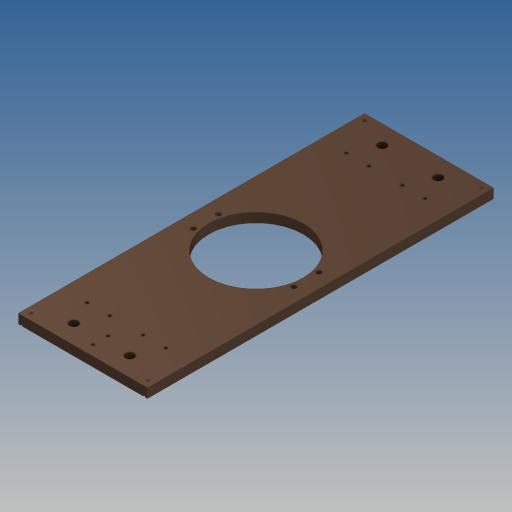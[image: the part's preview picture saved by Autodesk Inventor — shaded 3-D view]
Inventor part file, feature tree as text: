
AUTODESK INVENTOR PART (.ipt)
format: ipt  version: 2023.3 (Build 273359000, 359)  size: 237,056 bytes
history: native  units: mm
features: sketch x8, hole x6, extrude x2
ambient origin geometry x8: Origin, YZ Plane, XZ Plane, XY Plane, X Axis, Y Axis, Z Axis, Center Point
bodies: Body1 (feature_tree)
feature tree (16):
  extrude  "Extrusion1"  Depth=205.0mm
  hole  "Bohrung1"  [1 undecoded]
  extrude  "Extrusion2"  Depth=530.0mm
  hole  "Bohrung6"  [1 undecoded]
  hole  "Bohrung7"  [1 undecoded]
  hole  "Bohrung8"  [1 undecoded]
  hole  "Bohrung9"  [1 undecoded]
  hole  "Bohrung10"  [1 undecoded]
  sketch  "Skizze2"  dims[d8=150.0mm d9=205.0mm]
  sketch  "Skizze3"  dims[d10=550.0mm d11=15.0mm d12=0.0mm]
  sketch  "Skizze6"  dims[d13=185.0mm d14=530.0mm]
  sketch  "Skizze7"  dims[d15=4.917mm d16=20.0mm d17=4.0mm d18=2.0mm d19=90.0deg d20=8.0mm d21=20.594885mm d68=2.5mm]
  sketch  "Skizze8"  dims[d70=2.5mm d72=2.5mm d73=0.0mm]
  sketch  "Skizze9"  dims[d74=160.0mm d75=40.0mm]
  sketch  "Skizze10"  dims[d76=8.0mm d77=10.0mm d78=4.0mm d79=2.0mm d80=90.0deg d81=14.2mm d82=20.594885mm d84=198.0mm]
  sketch  "Skizze11"  dims[d85=99.0mm d86=205.0mm d87=125.0mm d88=412.0mm d89=53.0mm d90=412.0mm d91=4.917mm d92=12.0mm d93=17.0mm d94=10.0mm d95=90.0deg d96=13.8mm d97=20.594885mm d98=490.0mm d99=58.0mm d100=14.0mm d101=51.0mm d102=17.0mm d103=10.0mm d104=90.0deg d105=13.8mm d106=20.594885mm d107=40.0mm d108=102.5mm d109=4.917mm d110=12.0mm d111=4.0mm d112=2.0mm d113=90.0deg d114=8.0mm d115=20.594885mm d116=16.0mm d117=102.5mm d118=102.5mm d119=16.0mm d120=5.0mm d121=12.0mm d122=4.0mm d123=2.0mm d124=90.0deg d125=8.0mm d126=20.594885mm]
note: 6 required parameter values undecoded (feature->parameter linkage not recoverable at this tier; creation-order binding heuristic only, values carry confidence <= 0.55)
